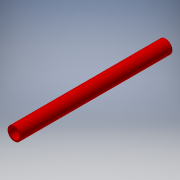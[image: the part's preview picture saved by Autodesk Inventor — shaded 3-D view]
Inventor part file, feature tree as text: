
AUTODESK INVENTOR PART (.ipt)
format: ipt  version: 2018 (Build 220112000, 112)  size: 107,008 bytes
history: native  units: in
note: dims shown in document units (in); Inventor stores cm internally (conversion verified against a paired STEP export)
features: extrude x1, sketch x1
ambient origin geometry x8: Origin, YZ Plane, XZ Plane, XY Plane, X Axis, Y Axis, Z Axis, Center Point
bodies: Solid1 (feature_tree)
feature tree (2):
  extrude  "Extrusion1"  Depth=14.698in
  sketch  "Sketch1"  dims[d0=1.315in d1=1.0in d2=14.698in d3=0.0in]
